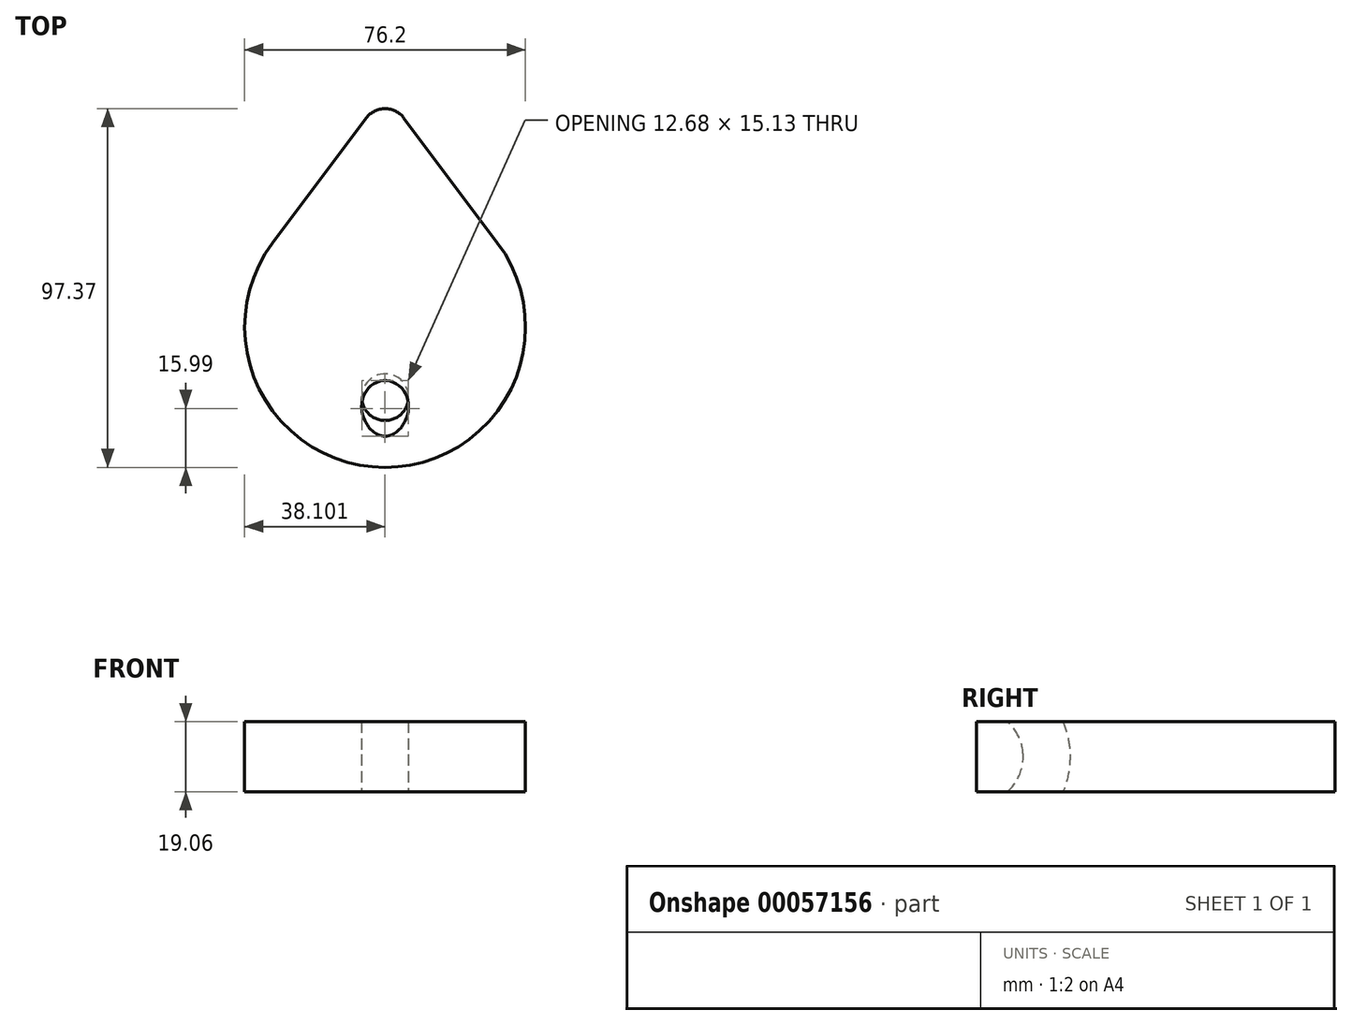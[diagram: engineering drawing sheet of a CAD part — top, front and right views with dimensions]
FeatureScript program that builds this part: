
annotation { "Feature Type Name" : "Feature", "Feature Type Description" : "" }
export const myFeature = defineFeature(function(context is Context, id is Id, definition is map)
    precondition{}
    {
        {
            var Q0;
            Q0=qCreatedBy(makeId("Top.planeOp"),FACE);
            var sketch = newSketch(context, id + "F0", { "sketchPlane" : qUnion([Q0])});
            skCircle(sketch, "E0", {"center": v(0, 0) * mm, "radius": 38.1 * mm, "construction": true});
            skPoint(sketch, "E1", {"position": v(0, 63.5) * mm});
            skLineSegment(sketch, "E2", {"start": v(-5.08, 56.73) * mm, "end": v(-30.48, 22.86) * mm, "construction": true});
            skLineSegment(sketch, "E3", {"start": v(5.08, 56.73) * mm, "end": v(30.48, 22.86) * mm, "construction": true});
            skArc(sketch, "E4.filletArc", {"start": v(5.08, 56.73) * mm, "mid": v(0, 59.27) * mm, "end": v(-5.08, 56.73) * mm, "construction": true});
            skArc(sketch, "E5", {"start": v(-30.48, 22.86) * mm, "mid": v(0, -38.1) * mm, "end": v(30.48, 22.86) * mm});
            skLineSegment(sketch, "E6", {"start": v(-30.48, 22.86) * mm, "end": v(-5.08, 56.73) * mm});
            skLineSegment(sketch, "E7", {"start": v(30.48, 22.86) * mm, "end": v(5.08, 56.73) * mm});
            skArc(sketch, "E8", {"start": v(-5.08, 56.73) * mm, "mid": v(0, 59.27) * mm, "end": v(5.08, 56.73) * mm});
            skSolve(sketch);
        }
        {
            var Q0;
            Q0 = qSketchRegion(id + "F0", true);
            extrude(context, id + "F1", {"entities" : qUnion([Q0]), "endBound" : BoundingType.SYMMETRIC, "depth" : 19.05 * mm});
        }
        {
            var Q0;
            Q0=qCreatedBy(makeId("Right.planeOp"),FACE);
            var sketch = newSketch(context, id + "F2", { "sketchPlane" : qUnion([Q0])});
            skLineSegment(sketch, "E9", {"start": v(-19.05, 0) * mm, "end": v(-19.05, 0) * mm});
            skLineSegment(sketch, "E10", {"start": v(-38.1, 19.05) * mm, "end": v(-75.56, 19.05) * mm});
            skLineSegment(sketch, "E11.MirrorCS", {"start": v(-38.1, -19.05) * mm, "end": v(-75.56, -19.05) * mm});
            skPoint(sketch, "E12.visualSharp", {"position": v(-19.05, 19.05) * mm});
            skArc(sketch, "E12.filletArc", {"start": v(-19.05, 0) * mm, "mid": v(-24.63, 13.47) * mm, "end": v(-38.1, 19.05) * mm});
            skPoint(sketch, "E13.visualSharp", {"position": v(-19.05, -19.05) * mm});
            skArc(sketch, "E13.filletArc", {"start": v(-38.1, -19.05) * mm, "mid": v(-24.63, -13.47) * mm, "end": v(-19.05, 0) * mm});
            skSolve(sketch);
        }
        {
            var Q0;
            Q0=qCreatedBy(makeId("Front.planeOp"),FACE);
            cPlane(context, id + "F3", {"entities" : qUnion([Q0]), "cplaneType" : CPlaneType.OFFSET, "offset" : 76.2 * mm, "width" : 152.4 * mm, "height" : 152.4 * mm});
        }
        {
            var Q0;
            Q0=qCreatedBy(id+"F3.planeOp",FACE);
            var sketch = newSketch(context, id + "F4", { "sketchPlane" : qUnion([Q0])});
            skCircle(sketch, "E14", {"center": v(0, 19.05) * mm, "radius": 6.35 * mm});
            skSolve(sketch);
        }
        {
            var Q0;
            Q0=makeQuery(id+"F4.imprint","IMPRINT",FACE,{"disambiguationData":[TD([[makeQuery(id+"F4.imprint","IMPRINT",EDGE,{"derivedFrom":sQuery(id+"F4.wireOp",EDGE,"E14")}),1.0]])]});
            var Q1;
            Q1=sQuery(id+"F2.wireOp",EDGE,"E10");
            var Q2;
            Q2=sQuery(id+"F2.wireOp",EDGE,"E12.filletArc");
            var Q3;
            Q3=sQuery(id+"F2.wireOp",EDGE,"E13.filletArc");
            var Q4;
            Q4=sQuery(id+"F2.wireOp",EDGE,"E11.MirrorCS");
            sweep(context, id + "F5", {"operationType" : NewBodyOperationType.REMOVE, "profiles" : qUnion([Q0]), "path" : qUnion([Q1, Q2, Q3, Q4])});
        }
    });
